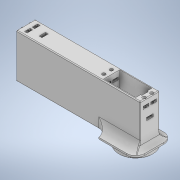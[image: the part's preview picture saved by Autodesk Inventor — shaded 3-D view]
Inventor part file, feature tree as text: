
AUTODESK INVENTOR PART (.ipt)
format: ipt  version: 2022 (Build 260153000, 153)  size: 1,192,960 bytes
history: native  units: mm
features: sketch x39, extrude x38, projected_geometry x14, fillet x13, other x10, pattern_circular x2, mirror x1
ambient origin geometry x8: Origin, YZ Plane, XZ Plane, XY Plane, X Axis, Y Axis, Z Axis, Center Point
bodies: Body1 (feature_tree)
feature tree (117):
  other  "Твердое тело1"
  extrude  "Выдавливание1"  Depth=29.25mm
  extrude  "Выдавливание2"  Depth=59.05mm
  extrude  "Выдавливание3"  Depth=15.0mm
  other  "РабПлоскость1"
  extrude  "Выдавливание4"  Depth=3.0mm
  other  "РабПлоскость2"
  other  "РабПлоскость3"
  other  "РабПлоскость5"
  extrude  "Выдавливание10"  Depth=41.0mm TaperAngle=0.0deg
  extrude  "Выдавливание11"  Depth=3.0mm TaperAngle=0.0deg
  fillet  "Сопряжение8"  Radius=4.2mm
  extrude  "Выдавливание12"  Depth=20.0mm TaperAngle=0.0deg
  fillet  "Сопряжение9"  [1 undecoded]
  mirror  "Зеркальное отражение2"
  extrude  "Выдавливание13"  Depth=7.15mm
  extrude  "Выдавливание15"  Depth=20.0mm
  sketch  "Эскиз18"
  other  "РабОсь1"
  extrude  "Выдавливание16"  Depth=3.25mm TaperAngle=0.0deg
  fillet  "Сопряжение12"  Radius=7.0mm
  pattern_circular  "Круговой массив1"  [2 undecoded]
  fillet  "Сопряжение14"  Radius=4.0mm
  extrude  "Выдавливание24"  Depth=1.95mm
  extrude  "Выдавливание25"  Depth=10.0mm
  extrude  "Выдавливание26"  Depth=2.0mm
  other  "РабПлоскость8"
  extrude  "Выдавливание27"  Depth=1.5mm TaperAngle=0.0deg
  extrude  "Выдавливание28"  Depth=1.0mm
  extrude  "Выдавливание29"  Depth=0.2mm
  extrude  "Выдавливание30"  Depth=19.0mm
  extrude  "Выдавливание31"  Depth=68.0mm
  extrude  "Выдавливание32"  Depth=3.5mm
  sketch  "Эскиз36"
  other  "РабТочка1"
  extrude  "Выдавливание33"  Depth=5.0mm
  extrude  "Выдавливание34"  Depth=4.1mm
  extrude  "Выдавливание35"  Depth=7.95mm
  extrude  "Выдавливание36"  Depth=28.1mm
  extrude  "Выдавливание37"  Depth=4.0mm TaperAngle=0.0deg
  other  "РабПлоскость9"
  extrude  "Выдавливание38"  Depth=18.75mm
  extrude  "Выдавливание39"  Depth=37.8mm
  extrude  "Выдавливание40"  Depth=2.0mm
  extrude  "Выдавливание41"  Depth=6.0mm TaperAngle=0.0deg
  extrude  "Выдавливание42"  Depth=0.5mm
  fillet  "Сопряжение21"  Radius=5.4mm
  fillet  "Сопряжение22"  Radius=0.7mm
  fillet  "Сопряжение23"  Radius=120.0mm
  extrude  "Выдавливание43"  Depth=1.5mm
  fillet  "Сопряжение24"  Radius=47.7mm
  pattern_circular  "Круговой массив2"  [2 undecoded]
  fillet  "Сопряжение25"  Radius=6.0mm
  extrude  "Выдавливание44"  Depth=1.5mm
  fillet  "Сопряжение26"  Radius=4.0mm
  extrude  "Выдавливание17"  Depth=4.0mm
  fillet  "Сопряжение15"  Radius=35.2mm
  extrude  "Выдавливание18"  Depth=9.8mm
  extrude  "Выдавливание19"  Depth=6.15mm
  extrude  "Выдавливание20"  Depth=5.8mm TaperAngle=0.0deg
  extrude  "Выдавливание21"  Depth=13.0mm
  fillet  "Сопряжение16"  Radius=1.9mm
  extrude  "Выдавливание22"  Depth=7.5mm
  other  "РабПлоскость7"
  extrude  "Выдавливание23"  Depth=4.8mm
  fillet  "Сопряжение17"  Radius=3.0mm
  sketch  "Эскиз14"
  sketch  "Эскиз1"
  sketch  "Эскиз2"
  sketch  "Эскиз3"
  sketch  "Эскиз4"
  sketch  "Эскиз10"
  sketch  "Эскиз11"
  sketch  "Эскиз13"
  sketch  "Эскиз15"
  sketch  "Эскиз17"
  sketch  "Эскиз19"
  projected_geometry  "Спроецированная петля1"
  sketch  "Эскиз20"
  projected_geometry  "Спроецированная петля2"
  sketch  "Эскиз21"
  projected_geometry  "Спроецированная петля3"
  sketch  "Эскиз22"
  sketch  "Эскиз23"
  sketch  "Эскиз25"
  projected_geometry  "Спроецированная петля4"
  sketch  "Эскиз26"
  projected_geometry  "Спроецированная петля5"
  sketch  "Эскиз27"
  projected_geometry  "Спроецированная петля6"
  sketch  "Эскиз28"
  projected_geometry  "Спроецированная петля7"
  sketch  "Эскиз29"
  projected_geometry  "Спроецированная петля8"
  sketch  "Эскиз31"
  projected_geometry  "Спроецированная петля9"
  sketch  "Эскиз32"
  sketch  "Эскиз33"
  sketch  "Эскиз34"
  sketch  "Эскиз35"
  sketch  "Эскиз37"
  projected_geometry  "Спроецированная петля10"
  sketch  "Эскиз38"
  sketch  "Эскиз39"
  sketch  "Эскиз40"
  sketch  "Эскиз41"
  sketch  "Эскиз42"
  projected_geometry  "Спроецированная петля11"
  sketch  "Эскиз43"
  sketch  "Эскиз44"
  projected_geometry  "Спроецированная петля12"
  sketch  "Эскиз45"
  projected_geometry  "Спроецированная петля13"
  projected_geometry  "Спроецированная петля14"
  sketch  "Эскиз46"
  sketch  "Эскиз47"
  sketch  "Эскиз48"
note: 5 required parameter values undecoded (feature->parameter linkage not recoverable at this tier; creation-order binding heuristic only, values carry confidence <= 0.55)
